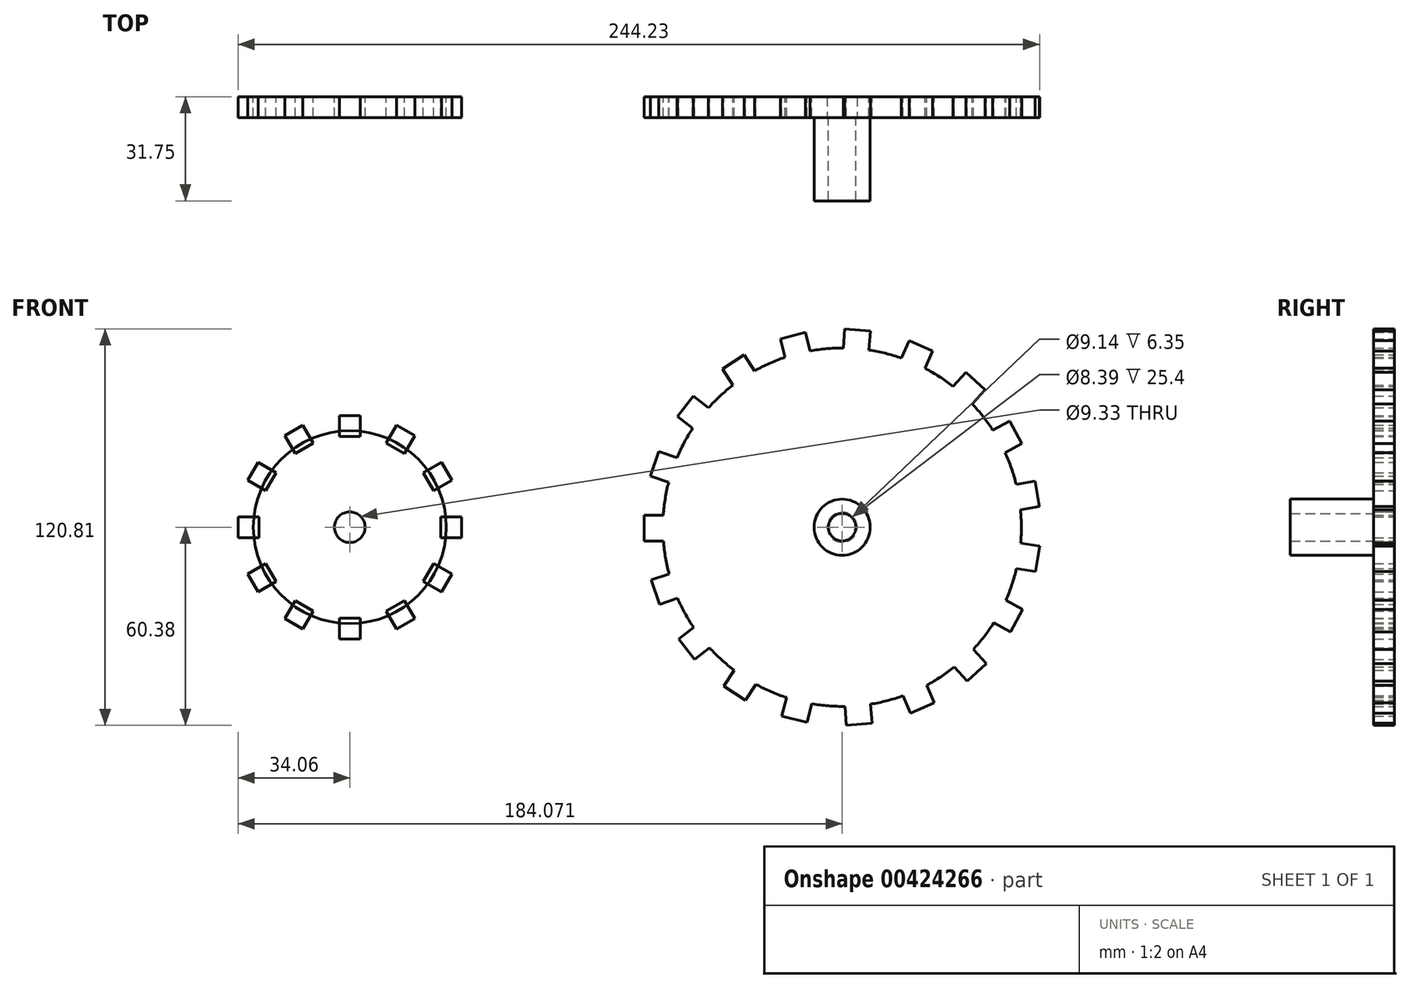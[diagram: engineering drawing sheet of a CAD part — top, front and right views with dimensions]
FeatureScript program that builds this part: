
annotation { "Feature Type Name" : "Feature", "Feature Type Description" : "" }
export const myFeature = defineFeature(function(context is Context, id is Id, definition is map)
    precondition{}
    {
        {
            var Q0;
            Q0=qCreatedBy(makeId("Front.planeOp"),FACE);
            var sketch = newSketch(context, id + "F0", { "sketchPlane" : qUnion([Q0])});
            skCircle(sketch, "E0", {"center": v(0, 0) * mm, "radius": 29.4 * mm});
            skSolve(sketch);
        }
        {
            var Q0;
            Q0 = qSketchRegion(id + "F0", true);
            extrude(context, id + "F1", {"entities" : qUnion([Q0]), "depth" : 6.35 * mm});
        }
        {
            var Q0;
            Q0=qCreatedBy(makeId("Front.planeOp"),FACE);
            var sketch = newSketch(context, id + "F2", { "sketchPlane" : qUnion([Q0])});
            skLineSegment(sketch, "E1.bottom", {"start": v(-3.18, 34.06) * mm, "end": v(3.18, 34.06) * mm});
            skLineSegment(sketch, "E1.top", {"start": v(-3.18, 27.71) * mm, "end": v(3.18, 27.71) * mm});
            skLineSegment(sketch, "E1.left", {"start": v(-3.18, 34.06) * mm, "end": v(-3.18, 27.71) * mm});
            skLineSegment(sketch, "E1.right", {"start": v(3.18, 34.06) * mm, "end": v(3.18, 27.71) * mm});
            skSolve(sketch);
        }
        {
            var Q0;
            Q0=makeQuery(id+"F2.imprint","IMPRINT",FACE,{"disambiguationData":[TD([[makeQuery(id+"F2.imprint","IMPRINT",EDGE,{"derivedFrom":sQuery(id+"F2.wireOp",EDGE,"E1.bottom")}),-1.0]])]});
            extrude(context, id + "F3", {"entities" : qUnion([Q0]), "depth" : 6.35 * mm});
        }
        {
            var Q0;
            Q0=makeQuery(id+"F3.opExtrude","SWEPT_BODY",BODY,{"disambiguationData":[OSD([sQuery(id+"F2.wireOp",EDGE,"E1.bottom"),sQuery(id+"F2.wireOp",EDGE,"E1.top"),sQuery(id+"F2.wireOp",EDGE,"E1.left"),sQuery(id+"F2.wireOp",EDGE,"E1.right")])]});
            var Q1;
            Q1=makeQuery(id+"F1.opExtrude","CAP_EDGE",EDGE,{"disambiguationData":[OSD([sQuery(id+"F0.wireOp",EDGE,"E0")])],"isStart":false});
            circularPattern(context, id + "F4", {"entities" : qUnion([Q0]), "axis" : qUnion([Q1]), "angle" : 360 * degree, "instanceCount" : 12, "equalSpace" : true});
        }
        {
            var Q0;
            Q0=makeQuery(id+"F1.opExtrude","CAP_FACE",FACE,{"disambiguationData":[OSD([sQuery(id+"F0.wireOp",EDGE,"E0")])],"isStart":true});
            var sketch = newSketch(context, id + "F5", { "sketchPlane" : qUnion([Q0])});
            skCircle(sketch, "E2", {"center": v(0, 0) * mm, "radius": 4.67 * mm});
            skSolve(sketch);
        }
        {
            var Q0;
            Q0=makeQuery(id+"F5.imprint","IMPRINT",FACE,{"disambiguationData":[TD([[makeQuery(id+"F5.imprint","IMPRINT",EDGE,{"derivedFrom":sQuery(id+"F5.wireOp",EDGE,"E2")}),1.0]])]});
            var Q1;
            Q1=sQuery(id+"F5.wireOp",EDGE,"E2");
            extrude(context, id + "F6", {"entities" : qUnion([Q0]), "operationType" : NewBodyOperationType.REMOVE, "surfaceEntities" : qUnion([Q1]), "oppositeDirection" : true, "depth" : 25.4 * mm});
        }
        {
            var Q0;
            Q0=qCreatedBy(makeId("Front.planeOp"),FACE);
            var sketch = newSketch(context, id + "F7", { "sketchPlane" : qUnion([Q0])});
            skCircle(sketch, "E3", {"center": v(150.01, 0) * mm, "radius": 54.61 * mm});
            skSolve(sketch);
        }
        {
            var Q0;
            Q0=qCreatedBy(makeId("Front.planeOp"),FACE);
            var sketch = newSketch(context, id + "F8", { "sketchPlane" : qUnion([Q0])});
            skLineSegment(sketch, "E4.bottom", {"start": v(96.07, 3.68) * mm, "end": v(89.72, 3.68) * mm});
            skLineSegment(sketch, "E4.top", {"start": v(96.07, -4.2) * mm, "end": v(89.72, -4.2) * mm});
            skLineSegment(sketch, "E4.left", {"start": v(96.07, 3.68) * mm, "end": v(96.07, -4.2) * mm});
            skLineSegment(sketch, "E4.right", {"start": v(89.72, 3.68) * mm, "end": v(89.72, -4.2) * mm});
            skSolve(sketch);
        }
        {
            var Q0;
            Q0=makeQuery(id+"F7.imprint","IMPRINT",FACE,{"disambiguationData":[TD([[makeQuery(id+"F7.imprint","IMPRINT",EDGE,{"derivedFrom":sQuery(id+"F7.wireOp",EDGE,"E3")}),1.0]])]});
            extrude(context, id + "F9", {"entities" : qUnion([Q0]), "depth" : 6.35 * mm});
        }
        {
            var Q0;
            Q0=makeQuery(id+"F8.imprint","IMPRINT",FACE,{"disambiguationData":[TD([[makeQuery(id+"F8.imprint","IMPRINT",EDGE,{"derivedFrom":sQuery(id+"F8.wireOp",EDGE,"E4.bottom")}),1.0]])]});
            extrude(context, id + "F10", {"entities" : qUnion([Q0]), "depth" : 6.35 * mm});
        }
        {
            var Q0;
            Q0=makeQuery(id+"F10.opExtrude","SWEPT_BODY",BODY,{"disambiguationData":[OSD([sQuery(id+"F8.wireOp",EDGE,"E4.bottom"),sQuery(id+"F8.wireOp",EDGE,"E4.top"),sQuery(id+"F8.wireOp",EDGE,"E4.left"),sQuery(id+"F8.wireOp",EDGE,"E4.right")])]});
            var Q1;
            Q1=makeQuery(id+"F9.opExtrude","CAP_EDGE",EDGE,{"disambiguationData":[OSD([sQuery(id+"F7.wireOp",EDGE,"E3")])],"isStart":false});
            circularPattern(context, id + "F11", {"entities" : qUnion([Q0]), "axis" : qUnion([Q1]), "angle" : 360 * degree, "instanceCount" : 19, "equalSpace" : true});
        }
        {
            var Q0;
            {var subQ0=makeQuery(id+"F10.opExtrude","CAP_FACE",FACE,{"disambiguationData":[OSD([sQuery(id+"F8.wireOp",EDGE,"ZRbgPriN-CiNv-fjNI-RmIJ-Uftv0Wc6BVWd.bottom"),sQuery(id+"F8.wireOp",EDGE,"ZRbgPriN-CiNv-fjNI-RmIJ-Uftv0Wc6BVWd.top"),sQuery(id+"F8.wireOp",EDGE,"ZRbgPriN-CiNv-fjNI-RmIJ-Uftv0Wc6BVWd.left"),sQuery(id+"F8.wireOp",EDGE,"ZRbgPriN-CiNv-fjNI-RmIJ-Uftv0Wc6BVWd.right")])],"isStart":false});Q0=makeQuery(id+"FukEfEByewJuotJ_4.opBoolean","MERGE",FACE,{"derivedFrom":[makeQuery(id+"F9.opExtrude","CAP_FACE",FACE,{"disambiguationData":[OSD([sQuery(id+"F7.wireOp",EDGE,"E3")])],"isStart":false}),subQ0,makeQuery(id+"F11.opPattern","COPY",FACE,{"derivedFrom":subQ0,"instanceName":"1"}),makeQuery(id+"F11.opPattern","COPY",FACE,{"derivedFrom":subQ0,"instanceName":"2"}),makeQuery(id+"F11.opPattern","COPY",FACE,{"derivedFrom":subQ0,"instanceName":"3"}),makeQuery(id+"F11.opPattern","COPY",FACE,{"derivedFrom":subQ0,"instanceName":"4"}),makeQuery(id+"F11.opPattern","COPY",FACE,{"derivedFrom":subQ0,"instanceName":"5"}),makeQuery(id+"F11.opPattern","COPY",FACE,{"derivedFrom":subQ0,"instanceName":"6"}),makeQuery(id+"F11.opPattern","COPY",FACE,{"derivedFrom":subQ0,"instanceName":"7"}),makeQuery(id+"F11.opPattern","COPY",FACE,{"derivedFrom":subQ0,"instanceName":"8"}),makeQuery(id+"F11.opPattern","COPY",FACE,{"derivedFrom":subQ0,"instanceName":"9"}),makeQuery(id+"F11.opPattern","COPY",FACE,{"derivedFrom":subQ0,"instanceName":"10"}),makeQuery(id+"F11.opPattern","COPY",FACE,{"derivedFrom":subQ0,"instanceName":"11"})]});}
            var sketch = newSketch(context, id + "F12", { "sketchPlane" : qUnion([Q0])});
            skCircle(sketch, "E5", {"center": v(150.01, 0) * mm, "radius": 4.57 * mm});
            skSolve(sketch);
        }
        {
            var Q0;
            Q0=makeQuery(id+"F12.imprint","IMPRINT",FACE,{"disambiguationData":[TD([[makeQuery(id+"F12.imprint","IMPRINT",EDGE,{"derivedFrom":sQuery(id+"F12.wireOp",EDGE,"E5")}),1.0]])]});
            var Q1;
            Q1=sQuery(id+"F12.wireOp",EDGE,"E5");
            extrude(context, id + "F13", {"entities" : qUnion([Q0]), "operationType" : NewBodyOperationType.REMOVE, "surfaceEntities" : qUnion([Q1]), "oppositeDirection" : true, "depth" : 25.4 * mm});
        }
        {
            var Q0;
            Q0=makeQuery(id+"F9.opExtrude","SWEPT_BODY",BODY,{"disambiguationData":[OSD([sQuery(id+"F7.wireOp",EDGE,"E3")])]});
            var Q1;
            Q1=makeQuery(id+"F10.opExtrude","SWEPT_BODY",BODY,{"disambiguationData":[OSD([sQuery(id+"F8.wireOp",EDGE,"E4.bottom"),sQuery(id+"F8.wireOp",EDGE,"E4.top"),sQuery(id+"F8.wireOp",EDGE,"E4.left"),sQuery(id+"F8.wireOp",EDGE,"E4.right")])]});
            var Q2;
            Q2=makeQuery(id+"F11.opPattern","COPY",BODY,{"derivedFrom":makeQuery(id+"F10.opExtrude","SWEPT_BODY",BODY,{"disambiguationData":[OSD([sQuery(id+"F8.wireOp",EDGE,"E4.bottom"),sQuery(id+"F8.wireOp",EDGE,"E4.top"),sQuery(id+"F8.wireOp",EDGE,"E4.left"),sQuery(id+"F8.wireOp",EDGE,"E4.right")])]}),"instanceName":"1"});
            var Q3;
            Q3=makeQuery(id+"F11.opPattern","COPY",BODY,{"derivedFrom":makeQuery(id+"F10.opExtrude","SWEPT_BODY",BODY,{"disambiguationData":[OSD([sQuery(id+"F8.wireOp",EDGE,"E4.bottom"),sQuery(id+"F8.wireOp",EDGE,"E4.top"),sQuery(id+"F8.wireOp",EDGE,"E4.left"),sQuery(id+"F8.wireOp",EDGE,"E4.right")])]}),"instanceName":"2"});
            var Q4;
            Q4=makeQuery(id+"F11.opPattern","COPY",BODY,{"derivedFrom":makeQuery(id+"F10.opExtrude","SWEPT_BODY",BODY,{"disambiguationData":[OSD([sQuery(id+"F8.wireOp",EDGE,"E4.bottom"),sQuery(id+"F8.wireOp",EDGE,"E4.top"),sQuery(id+"F8.wireOp",EDGE,"E4.left"),sQuery(id+"F8.wireOp",EDGE,"E4.right")])]}),"instanceName":"3"});
            var Q5;
            Q5=makeQuery(id+"F11.opPattern","COPY",BODY,{"derivedFrom":makeQuery(id+"F10.opExtrude","SWEPT_BODY",BODY,{"disambiguationData":[OSD([sQuery(id+"F8.wireOp",EDGE,"E4.bottom"),sQuery(id+"F8.wireOp",EDGE,"E4.top"),sQuery(id+"F8.wireOp",EDGE,"E4.left"),sQuery(id+"F8.wireOp",EDGE,"E4.right")])]}),"instanceName":"4"});
            var Q6;
            Q6=makeQuery(id+"F11.opPattern","COPY",BODY,{"derivedFrom":makeQuery(id+"F10.opExtrude","SWEPT_BODY",BODY,{"disambiguationData":[OSD([sQuery(id+"F8.wireOp",EDGE,"E4.bottom"),sQuery(id+"F8.wireOp",EDGE,"E4.top"),sQuery(id+"F8.wireOp",EDGE,"E4.left"),sQuery(id+"F8.wireOp",EDGE,"E4.right")])]}),"instanceName":"5"});
            var Q7;
            Q7=makeQuery(id+"F11.opPattern","COPY",BODY,{"derivedFrom":makeQuery(id+"F10.opExtrude","SWEPT_BODY",BODY,{"disambiguationData":[OSD([sQuery(id+"F8.wireOp",EDGE,"E4.bottom"),sQuery(id+"F8.wireOp",EDGE,"E4.top"),sQuery(id+"F8.wireOp",EDGE,"E4.left"),sQuery(id+"F8.wireOp",EDGE,"E4.right")])]}),"instanceName":"6"});
            var Q8;
            Q8=makeQuery(id+"F11.opPattern","COPY",BODY,{"derivedFrom":makeQuery(id+"F10.opExtrude","SWEPT_BODY",BODY,{"disambiguationData":[OSD([sQuery(id+"F8.wireOp",EDGE,"E4.bottom"),sQuery(id+"F8.wireOp",EDGE,"E4.top"),sQuery(id+"F8.wireOp",EDGE,"E4.left"),sQuery(id+"F8.wireOp",EDGE,"E4.right")])]}),"instanceName":"7"});
            var Q9;
            Q9=makeQuery(id+"F11.opPattern","COPY",BODY,{"derivedFrom":makeQuery(id+"F10.opExtrude","SWEPT_BODY",BODY,{"disambiguationData":[OSD([sQuery(id+"F8.wireOp",EDGE,"E4.bottom"),sQuery(id+"F8.wireOp",EDGE,"E4.top"),sQuery(id+"F8.wireOp",EDGE,"E4.left"),sQuery(id+"F8.wireOp",EDGE,"E4.right")])]}),"instanceName":"8"});
            var Q10;
            Q10=makeQuery(id+"F11.opPattern","COPY",BODY,{"derivedFrom":makeQuery(id+"F10.opExtrude","SWEPT_BODY",BODY,{"disambiguationData":[OSD([sQuery(id+"F8.wireOp",EDGE,"E4.bottom"),sQuery(id+"F8.wireOp",EDGE,"E4.top"),sQuery(id+"F8.wireOp",EDGE,"E4.left"),sQuery(id+"F8.wireOp",EDGE,"E4.right")])]}),"instanceName":"9"});
            var Q11;
            Q11=makeQuery(id+"F11.opPattern","COPY",BODY,{"derivedFrom":makeQuery(id+"F10.opExtrude","SWEPT_BODY",BODY,{"disambiguationData":[OSD([sQuery(id+"F8.wireOp",EDGE,"E4.bottom"),sQuery(id+"F8.wireOp",EDGE,"E4.top"),sQuery(id+"F8.wireOp",EDGE,"E4.left"),sQuery(id+"F8.wireOp",EDGE,"E4.right")])]}),"instanceName":"10"});
            var Q12;
            Q12=makeQuery(id+"F11.opPattern","COPY",BODY,{"derivedFrom":makeQuery(id+"F10.opExtrude","SWEPT_BODY",BODY,{"disambiguationData":[OSD([sQuery(id+"F8.wireOp",EDGE,"E4.bottom"),sQuery(id+"F8.wireOp",EDGE,"E4.top"),sQuery(id+"F8.wireOp",EDGE,"E4.left"),sQuery(id+"F8.wireOp",EDGE,"E4.right")])]}),"instanceName":"11"});
            var Q13;
            Q13=makeQuery(id+"F11.opPattern","COPY",BODY,{"derivedFrom":makeQuery(id+"F10.opExtrude","SWEPT_BODY",BODY,{"disambiguationData":[OSD([sQuery(id+"F8.wireOp",EDGE,"E4.bottom"),sQuery(id+"F8.wireOp",EDGE,"E4.top"),sQuery(id+"F8.wireOp",EDGE,"E4.left"),sQuery(id+"F8.wireOp",EDGE,"E4.right")])]}),"instanceName":"12"});
            var Q14;
            Q14=makeQuery(id+"F11.opPattern","COPY",BODY,{"derivedFrom":makeQuery(id+"F10.opExtrude","SWEPT_BODY",BODY,{"disambiguationData":[OSD([sQuery(id+"F8.wireOp",EDGE,"E4.bottom"),sQuery(id+"F8.wireOp",EDGE,"E4.top"),sQuery(id+"F8.wireOp",EDGE,"E4.left"),sQuery(id+"F8.wireOp",EDGE,"E4.right")])]}),"instanceName":"13"});
            var Q15;
            Q15=makeQuery(id+"F11.opPattern","COPY",BODY,{"derivedFrom":makeQuery(id+"F10.opExtrude","SWEPT_BODY",BODY,{"disambiguationData":[OSD([sQuery(id+"F8.wireOp",EDGE,"E4.bottom"),sQuery(id+"F8.wireOp",EDGE,"E4.top"),sQuery(id+"F8.wireOp",EDGE,"E4.left"),sQuery(id+"F8.wireOp",EDGE,"E4.right")])]}),"instanceName":"14"});
            var Q16;
            Q16=makeQuery(id+"F11.opPattern","COPY",BODY,{"derivedFrom":makeQuery(id+"F10.opExtrude","SWEPT_BODY",BODY,{"disambiguationData":[OSD([sQuery(id+"F8.wireOp",EDGE,"E4.bottom"),sQuery(id+"F8.wireOp",EDGE,"E4.top"),sQuery(id+"F8.wireOp",EDGE,"E4.left"),sQuery(id+"F8.wireOp",EDGE,"E4.right")])]}),"instanceName":"15"});
            var Q17;
            Q17=makeQuery(id+"F11.opPattern","COPY",BODY,{"derivedFrom":makeQuery(id+"F10.opExtrude","SWEPT_BODY",BODY,{"disambiguationData":[OSD([sQuery(id+"F8.wireOp",EDGE,"E4.bottom"),sQuery(id+"F8.wireOp",EDGE,"E4.top"),sQuery(id+"F8.wireOp",EDGE,"E4.left"),sQuery(id+"F8.wireOp",EDGE,"E4.right")])]}),"instanceName":"16"});
            var Q18;
            Q18=makeQuery(id+"F11.opPattern","COPY",BODY,{"derivedFrom":makeQuery(id+"F10.opExtrude","SWEPT_BODY",BODY,{"disambiguationData":[OSD([sQuery(id+"F8.wireOp",EDGE,"E4.bottom"),sQuery(id+"F8.wireOp",EDGE,"E4.top"),sQuery(id+"F8.wireOp",EDGE,"E4.left"),sQuery(id+"F8.wireOp",EDGE,"E4.right")])]}),"instanceName":"17"});
            booleanBodies(context, id + "F14", {"operationType" : BooleanOperationType.UNION, "tools" : qUnion([Q0, Q1, Q2, Q3, Q4, Q5, Q6, Q7, Q8, Q9, Q10, Q11, Q12, Q13, Q14, Q15, Q16, Q17, Q18])});
        }
        {
            var Q0;
            Q0=makeQuery(id+"F11.opPattern","COPY",BODY,{"derivedFrom":makeQuery(id+"F10.opExtrude","SWEPT_BODY",BODY,{"disambiguationData":[OSD([sQuery(id+"F8.wireOp",EDGE,"E4.bottom"),sQuery(id+"F8.wireOp",EDGE,"E4.top"),sQuery(id+"F8.wireOp",EDGE,"E4.left"),sQuery(id+"F8.wireOp",EDGE,"E4.right")])]}),"instanceName":"18"});
            var Q1;
            Q1=makeQuery(id+"F9.opExtrude","SWEPT_BODY",BODY,{"disambiguationData":[OSD([sQuery(id+"F7.wireOp",EDGE,"E3")])]});
            booleanBodies(context, id + "F15", {"operationType" : BooleanOperationType.UNION, "tools" : qUnion([Q0, Q1])});
        }
        {
            var Q0;
            {var subQ0=makeQuery(id+"F10.opExtrude","CAP_FACE",FACE,{"disambiguationData":[OSD([sQuery(id+"F8.wireOp",EDGE,"E4.bottom"),sQuery(id+"F8.wireOp",EDGE,"E4.top"),sQuery(id+"F8.wireOp",EDGE,"E4.left"),sQuery(id+"F8.wireOp",EDGE,"E4.right")])],"isStart":false});Q0=makeQuery(id+"F15.opBoolean","MERGE",FACE,{"derivedFrom":[makeQuery(id+"F11.opPattern","COPY",FACE,{"derivedFrom":subQ0,"instanceName":"18"}),makeQuery(id+"F14.opBoolean","MERGE",FACE,{"derivedFrom":[subQ0,makeQuery(id+"F11.opPattern","COPY",FACE,{"derivedFrom":subQ0,"instanceName":"1"}),makeQuery(id+"F11.opPattern","COPY",FACE,{"derivedFrom":subQ0,"instanceName":"2"}),makeQuery(id+"F11.opPattern","COPY",FACE,{"derivedFrom":subQ0,"instanceName":"3"}),makeQuery(id+"F11.opPattern","COPY",FACE,{"derivedFrom":subQ0,"instanceName":"4"}),makeQuery(id+"F11.opPattern","COPY",FACE,{"derivedFrom":subQ0,"instanceName":"5"}),makeQuery(id+"F11.opPattern","COPY",FACE,{"derivedFrom":subQ0,"instanceName":"6"}),makeQuery(id+"F11.opPattern","COPY",FACE,{"derivedFrom":subQ0,"instanceName":"7"}),makeQuery(id+"F11.opPattern","COPY",FACE,{"derivedFrom":subQ0,"instanceName":"8"}),makeQuery(id+"F11.opPattern","COPY",FACE,{"derivedFrom":subQ0,"instanceName":"9"}),makeQuery(id+"F11.opPattern","COPY",FACE,{"derivedFrom":subQ0,"instanceName":"10"}),makeQuery(id+"F11.opPattern","COPY",FACE,{"derivedFrom":subQ0,"instanceName":"11"}),makeQuery(id+"F11.opPattern","COPY",FACE,{"derivedFrom":subQ0,"instanceName":"12"}),makeQuery(id+"F11.opPattern","COPY",FACE,{"derivedFrom":subQ0,"instanceName":"13"}),makeQuery(id+"F11.opPattern","COPY",FACE,{"derivedFrom":subQ0,"instanceName":"14"}),makeQuery(id+"F11.opPattern","COPY",FACE,{"derivedFrom":subQ0,"instanceName":"15"}),makeQuery(id+"F11.opPattern","COPY",FACE,{"derivedFrom":subQ0,"instanceName":"16"}),makeQuery(id+"F11.opPattern","COPY",FACE,{"derivedFrom":subQ0,"instanceName":"17"}),makeQuery(id+"F9.opExtrude","CAP_FACE",FACE,{"disambiguationData":[OSD([sQuery(id+"F7.wireOp",EDGE,"E3")])],"isStart":false})]})]});}
            var sketch = newSketch(context, id + "F16", { "sketchPlane" : qUnion([Q0])});
            skCircle(sketch, "E6", {"center": v(150.01, 0) * mm, "radius": 4.2 * mm});
            skCircle(sketch, "E7", {"center": v(150.01, 0) * mm, "radius": 8.56 * mm});
            skSolve(sketch);
        }
        {
            var Q0;
            Q0 = qSketchRegion(id + "F16", true);
            extrude(context, id + "F17", {"entities" : qUnion([Q0]), "operationType" : NewBodyOperationType.ADD, "depth" : 25.4 * mm});
        }
    });
